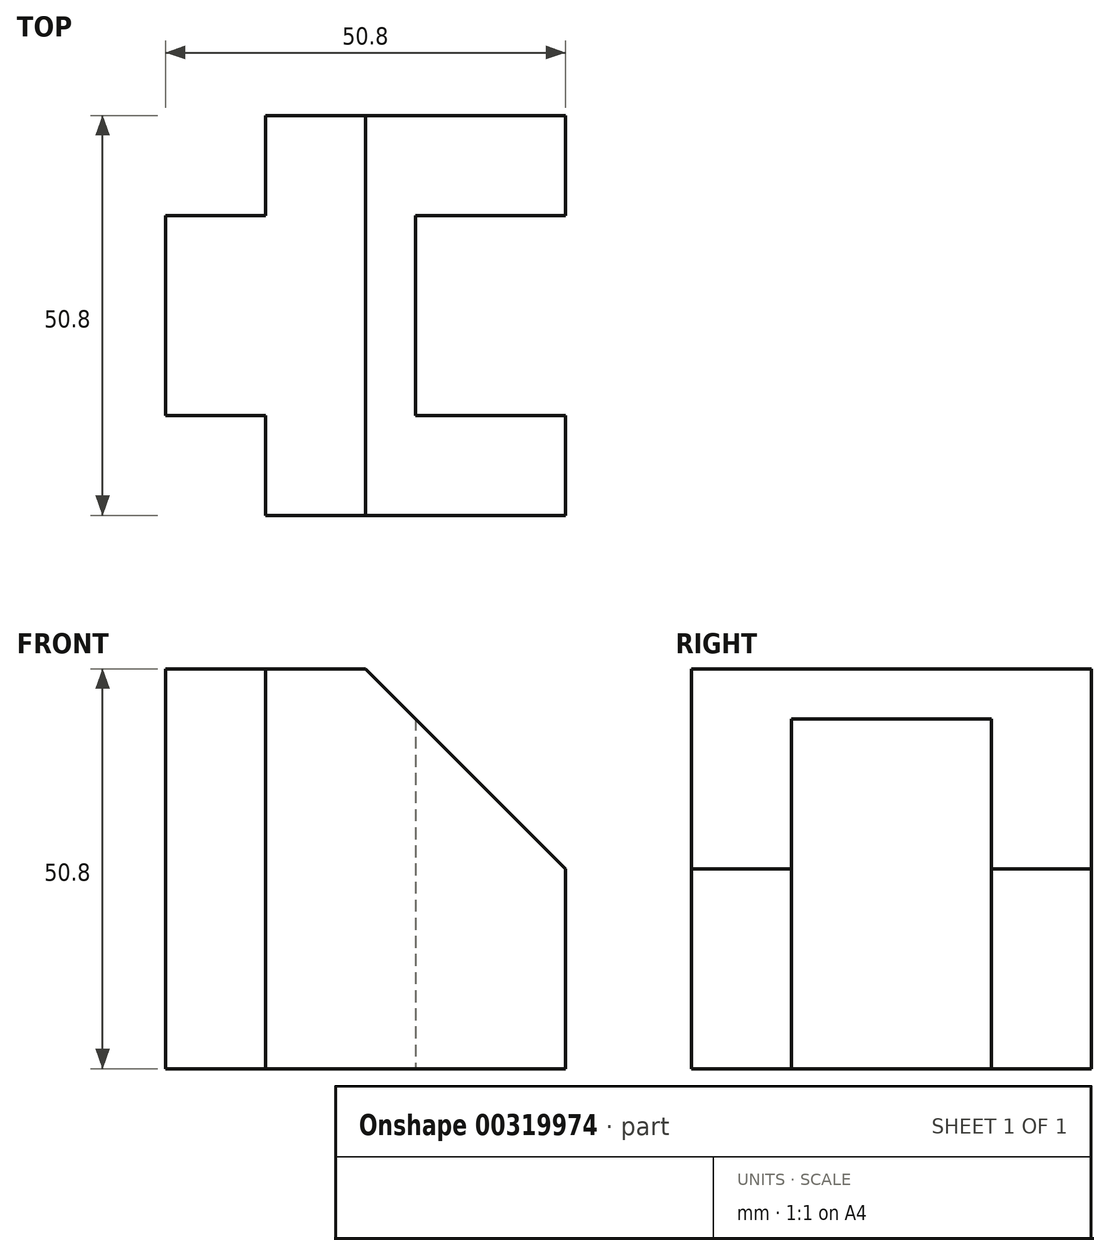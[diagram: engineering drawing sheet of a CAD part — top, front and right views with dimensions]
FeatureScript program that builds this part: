
annotation { "Feature Type Name" : "Feature", "Feature Type Description" : "" }
export const myFeature = defineFeature(function(context is Context, id is Id, definition is map)
    precondition{}
    {
        {
            var Q0;
            Q0=qCreatedBy(makeId("Top.planeOp"),FACE);
            var sketch = newSketch(context, id + "F0", { "sketchPlane" : qUnion([Q0])});
            skLineSegment(sketch, "E0", {"start": v(0, 0) * mm, "end": v(12.7, 0) * mm});
            skLineSegment(sketch, "E1", {"start": v(12.7, 0) * mm, "end": v(12.7, -12.7) * mm});
            skLineSegment(sketch, "E2", {"start": v(12.7, -12.7) * mm, "end": v(50.8, -12.7) * mm});
            skLineSegment(sketch, "E3", {"start": v(50.8, -12.7) * mm, "end": v(50.8, 0) * mm});
            skLineSegment(sketch, "E4", {"start": v(50.8, 0) * mm, "end": v(31.75, 0) * mm});
            skLineSegment(sketch, "E5", {"start": v(31.75, 0) * mm, "end": v(31.75, 25.4) * mm});
            skLineSegment(sketch, "E6", {"start": v(31.75, 25.4) * mm, "end": v(50.8, 25.4) * mm});
            skLineSegment(sketch, "E7", {"start": v(50.8, 25.4) * mm, "end": v(50.8, 38.1) * mm});
            skLineSegment(sketch, "E8", {"start": v(50.8, 38.1) * mm, "end": v(12.7, 38.1) * mm});
            skLineSegment(sketch, "E9", {"start": v(12.7, 38.1) * mm, "end": v(12.7, 25.4) * mm});
            skLineSegment(sketch, "E10", {"start": v(12.7, 25.4) * mm, "end": v(0, 25.4) * mm});
            skLineSegment(sketch, "E11", {"start": v(0, 25.4) * mm, "end": v(0, 0) * mm});
            skSolve(sketch);
        }
        {
            var Q0;
            Q0=makeQuery(id+"F0.imprint","IMPRINT",FACE,{"disambiguationData":[TD([[makeQuery(id+"F0.imprint","IMPRINT",EDGE,{"derivedFrom":sQuery(id+"F0.wireOp",EDGE,"E0")}),1.0]])]});
            extrude(context, id + "F1", {"entities" : qUnion([Q0]), "depth" : 50.8 * mm});
        }
        {
            var Q0;
            Q0=makeQuery(id+"F1.opExtrude","SWEPT_FACE",FACE,{"disambiguationData":[OSD([sQuery(id+"F0.wireOp",EDGE,"E2")])]});
            var sketch = newSketch(context, id + "F2", { "sketchPlane" : qUnion([Q0])});
            skLineSegment(sketch, "E12", {"start": v(50.8, 50.8) * mm, "end": v(25.4, 50.8) * mm});
            skLineSegment(sketch, "E13", {"start": v(50.8, 50.8) * mm, "end": v(50.8, 25.4) * mm});
            skLineSegment(sketch, "E14", {"start": v(50.8, 25.4) * mm, "end": v(25.4, 50.8) * mm});
            skSolve(sketch);
        }
        {
            var Q0;
            Q0=makeQuery(id+"F2.imprint","IMPRINT",FACE,{"disambiguationData":[TD([[makeQuery(id+"F2.imprint","IMPRINT",EDGE,{"derivedFrom":sQuery(id+"F2.wireOp",EDGE,"E12")}),-1.0]])]});
            extrude(context, id + "F3", {"entities" : qUnion([Q0]), "operationType" : NewBodyOperationType.REMOVE, "endBound" : BoundingType.THROUGH_ALL, "oppositeDirection" : true, "depth" : 25.4 * mm});
        }
    });
